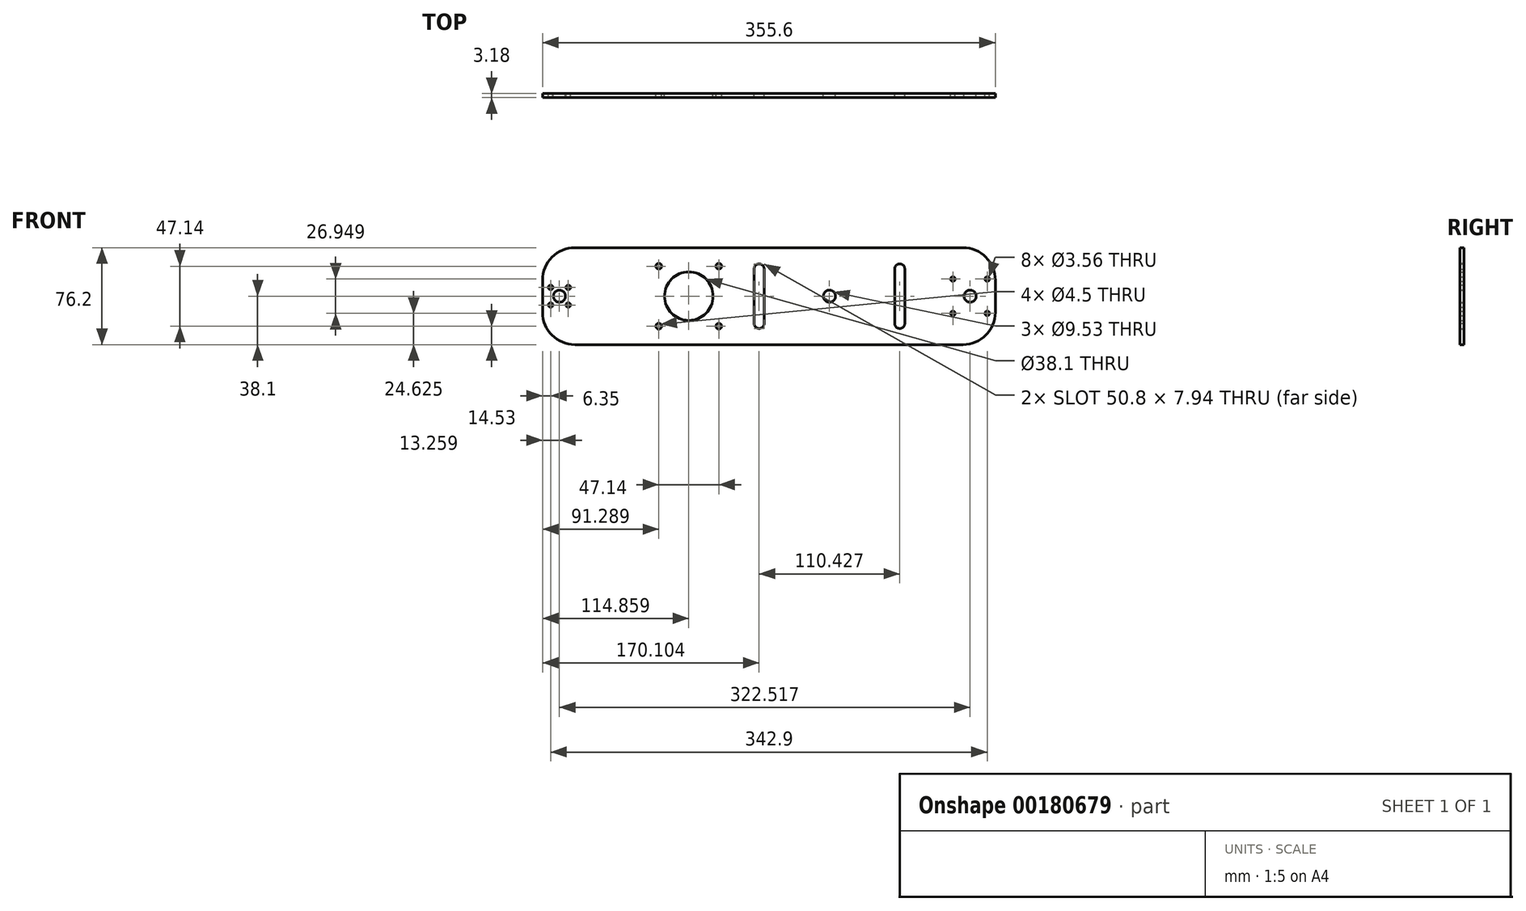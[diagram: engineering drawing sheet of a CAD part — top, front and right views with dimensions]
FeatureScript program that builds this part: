
annotation { "Feature Type Name" : "Feature", "Feature Type Description" : "" }
export const myFeature = defineFeature(function(context is Context, id is Id, definition is map)
    precondition{}
    {
        {
            var Q0;
            Q0=qCreatedBy(makeId("Front.planeOp"),FACE);
            var sketch = newSketch(context, id + "F0", { "sketchPlane" : qUnion([Q0])});
            skLineSegment(sketch, "E0.bottom", {"start": v(152.4, 38.1) * mm, "end": v(-152.4, 38.1) * mm});
            skLineSegment(sketch, "E0.top", {"start": v(152.4, -38.1) * mm, "end": v(-152.4, -38.1) * mm});
            skLineSegment(sketch, "E0.left", {"start": v(177.8, 12.7) * mm, "end": v(177.8, -12.7) * mm});
            skLineSegment(sketch, "E0.right", {"start": v(-177.8, 12.7) * mm, "end": v(-177.8, -12.7) * mm});
            skPoint(sketch, "E0.middle", {"position": v(0, 0) * mm});
            skCircle(sketch, "E1", {"center": v(-164.54, 0) * mm, "radius": 4.76 * mm});
            skCircle(sketch, "E2", {"center": v(-171.45, 6.9) * mm, "radius": 1.78 * mm});
            skCircle(sketch, "E3.0.1.0", {"center": v(-171.45, -6.9) * mm, "radius": 1.78 * mm});
            skCircle(sketch, "E3.1.0.0", {"center": v(-157.63, 6.9) * mm, "radius": 1.78 * mm});
            skCircle(sketch, "E3.1.1.0", {"center": v(-157.63, -6.9) * mm, "radius": 1.78 * mm});
            skLineSegment(sketch, "E3.direction1", {"start": v(-171.45, 6.9) * mm, "end": v(-157.63, 6.9) * mm, "construction": true});
            skLineSegment(sketch, "E3.direction2", {"start": v(-171.45, 6.9) * mm, "end": v(-171.45, -6.9) * mm, "construction": true});
            skCircle(sketch, "E4", {"center": v(-62.94, 0) * mm, "radius": 19.05 * mm});
            skCircle(sketch, "E5", {"center": v(-86.51, 23.57) * mm, "radius": 2.25 * mm});
            skCircle(sketch, "E6.0.1.0", {"center": v(-86.51, -23.57) * mm, "radius": 2.25 * mm});
            skCircle(sketch, "E6.1.0.0", {"center": v(-39.37, 23.57) * mm, "radius": 2.25 * mm});
            skCircle(sketch, "E6.1.1.0", {"center": v(-39.37, -23.57) * mm, "radius": 2.25 * mm});
            skLineSegment(sketch, "E6.direction1", {"start": v(-86.51, 23.57) * mm, "end": v(-39.37, 23.57) * mm, "construction": true});
            skLineSegment(sketch, "E6.direction2", {"start": v(-86.51, 23.57) * mm, "end": v(-86.51, -23.57) * mm, "construction": true});
            skCircle(sketch, "E7", {"center": v(47.49, 0) * mm, "radius": 4.76 * mm});
            skCircle(sketch, "E8", {"center": v(157.98, 0) * mm, "radius": 4.76 * mm});
            skCircle(sketch, "E9", {"center": v(144.5, 13.47) * mm, "radius": 1.78 * mm});
            skCircle(sketch, "E10.0.1.0", {"center": v(144.5, -13.47) * mm, "radius": 1.78 * mm});
            skCircle(sketch, "E10.1.0.0", {"center": v(171.45, 13.47) * mm, "radius": 1.78 * mm});
            skCircle(sketch, "E10.1.1.0", {"center": v(171.45, -13.47) * mm, "radius": 1.78 * mm});
            skLineSegment(sketch, "E10.direction1", {"start": v(144.5, 13.47) * mm, "end": v(171.45, 13.47) * mm, "construction": true});
            skLineSegment(sketch, "E10.direction2", {"start": v(144.5, 13.47) * mm, "end": v(144.5, -13.47) * mm, "construction": true});
            skLineSegment(sketch, "E11.bottom", {"start": v(-7.7, -25.4) * mm, "end": v(-7.7, -25.4) * mm});
            skLineSegment(sketch, "E11.top", {"start": v(-7.7, 25.4) * mm, "end": v(-7.7, 25.4) * mm});
            skLineSegment(sketch, "E11.left", {"start": v(-3.73, -21.43) * mm, "end": v(-3.73, 21.43) * mm});
            skLineSegment(sketch, "E11.right", {"start": v(-11.66, -21.43) * mm, "end": v(-11.66, 21.43) * mm});
            skPoint(sketch, "E11.middle", {"position": v(-7.7, 0) * mm});
            skLineSegment(sketch, "E12.bottom", {"start": v(78.99, -25.4) * mm, "end": v(78.99, -25.4) * mm});
            skLineSegment(sketch, "E12.top", {"start": v(78.99, 25.4) * mm, "end": v(78.99, 25.4) * mm});
            skLineSegment(sketch, "E12.left", {"start": v(106.7, -21.43) * mm, "end": v(106.7, 21.43) * mm});
            skLineSegment(sketch, "E12.right", {"start": v(98.76, -21.43) * mm, "end": v(98.76, 21.43) * mm});
            skPoint(sketch, "E12.middle", {"position": v(102.73, 0) * mm});
            skPoint(sketch, "E13.visualSharp", {"position": v(-11.66, -25.4) * mm});
            skArc(sketch, "E13.filletArc", {"start": v(-11.66, -21.43) * mm, "mid": v(-10.5, -24.24) * mm, "end": v(-7.7, -25.4) * mm});
            skPoint(sketch, "E14.visualSharp", {"position": v(-3.73, -25.4) * mm});
            skArc(sketch, "E14.filletArc", {"start": v(-7.7, -25.4) * mm, "mid": v(-4.89, -24.24) * mm, "end": v(-3.73, -21.43) * mm});
            skPoint(sketch, "E15.visualSharp", {"position": v(-11.66, 25.4) * mm});
            skArc(sketch, "E15.filletArc", {"start": v(-7.7, 25.4) * mm, "mid": v(-10.5, 24.24) * mm, "end": v(-11.66, 21.43) * mm});
            skPoint(sketch, "E16.visualSharp", {"position": v(-3.73, 25.4) * mm});
            skArc(sketch, "E16.filletArc", {"start": v(-3.73, 21.43) * mm, "mid": v(-4.89, 24.24) * mm, "end": v(-7.7, 25.4) * mm});
            skPoint(sketch, "E17.visualSharp", {"position": v(98.76, -25.4) * mm});
            skArc(sketch, "E17.filletArc", {"start": v(98.76, -21.43) * mm, "mid": v(99.92, -24.24) * mm, "end": v(102.73, -25.4) * mm});
            skPoint(sketch, "E18.visualSharp", {"position": v(106.7, -25.4) * mm});
            skArc(sketch, "E18.filletArc", {"start": v(102.73, -25.4) * mm, "mid": v(105.54, -24.24) * mm, "end": v(106.7, -21.43) * mm});
            skPoint(sketch, "E19.visualSharp", {"position": v(98.76, 25.4) * mm});
            skArc(sketch, "E19.filletArc", {"start": v(102.73, 25.4) * mm, "mid": v(99.92, 24.24) * mm, "end": v(98.76, 21.43) * mm});
            skPoint(sketch, "E20.visualSharp", {"position": v(106.7, 25.4) * mm});
            skArc(sketch, "E20.filletArc", {"start": v(106.7, 21.43) * mm, "mid": v(105.54, 24.24) * mm, "end": v(102.73, 25.4) * mm});
            skPoint(sketch, "E21.visualSharp", {"position": v(-177.8, 38.1) * mm});
            skArc(sketch, "E21.filletArc", {"start": v(-152.4, 38.1) * mm, "mid": v(-170.36, 30.66) * mm, "end": v(-177.8, 12.7) * mm});
            skPoint(sketch, "E22.visualSharp", {"position": v(-177.8, -38.1) * mm});
            skArc(sketch, "E22.filletArc", {"start": v(-177.8, -12.7) * mm, "mid": v(-170.36, -30.66) * mm, "end": v(-152.4, -38.1) * mm});
            skPoint(sketch, "E23.visualSharp", {"position": v(177.8, 38.1) * mm});
            skArc(sketch, "E23.filletArc", {"start": v(177.8, 12.7) * mm, "mid": v(170.36, 30.66) * mm, "end": v(152.4, 38.1) * mm});
            skPoint(sketch, "E24.visualSharp", {"position": v(177.8, -38.1) * mm});
            skArc(sketch, "E24.filletArc", {"start": v(152.4, -38.1) * mm, "mid": v(170.36, -30.66) * mm, "end": v(177.8, -12.7) * mm});
            skSolve(sketch);
        }
        {
            var Q0;
            Q0=makeQuery(id+"F0.imprint","IMPRINT",FACE,{"disambiguationData":[TD([[makeQuery(id+"F0.imprint","IMPRINT",EDGE,{"derivedFrom":sQuery(id+"F0.wireOp",EDGE,"E0.bottom")}),1.0]])]});
            extrude(context, id + "F1", {"entities" : qUnion([Q0]), "depth" : 3.17 * mm});
        }
    });
